# Revit family: Hager-Panelboard_JN_Top-Bottom_Meter_Enclosure-UK-en
name_source: partatom
category: Electrical Equipment
units: mm (PartAtom-declared; Revit-internal decimal feet)

## family parameters
Cut with Voids When Loaded = No
Host = Face
Panel Configuration = Two Columns, Circuits Across
Part Type = Panelboard
Room Calculation Point = No
Round Connector Dimension = Use Diameter
Shared = No

## types (2) — shared parameters
Classification.Uniclass.Pr.Description = Control circuit device enclosures
Classification.Uniclass.Pr.Number = Pr_80_77_28_16
Default Elevation = 1219 mm
EF000003 - Mounting method = EV000384 - Surface mounted (plaster)
EF000007 - Colour = EV000154 - Other
EF000008 - Width = 710 mm
EF000049 - Depth = 160 mm  [stored 0.524934 ft]
EF000118 - With mounting plate = No
EF000339 - Type of cover = EV004216 - Door
EF001062 - EMC-version = No
EF001088 - Extension possible = No
EF001134 - DIN-rail = No
EF001596 - Material housing = EV000179 - Steel
EF004462 - Type of closure = EV000154 - Other
EF005474 - Degree of protection (IP) = EV009848 - IP2XC
EF006244 - Transparent cover/door = No
EF006306 - With lock = No
EF015776 - Earthing terminal block = Yes
EF015941 - Signal passing door = No
Ground Bus = No
HG000001 - Number of columns = 3
HG000002 - With door or cover = Yes
HG000003 - Range = Panelboard Meter Enclosures
HG000005 - Thickness = 3 mm  [stored 0.00984252 ft]
HG000018 - Cut-outs in left = No
HG000019 - Cut-outs in right = No
Manufacturer = Hager
Neutral Bus = No
Type Comments = Panelboard Meter Enclosures
zero-valued in all types: EF000218 - Built-in depth, EF000332 - Built-in height, EF000846 - Built-in width, EF001131 - Internal depth

## per-type parameters (varying)
| type | EF000040 - Height | EF000266 - Number of rows | EF002950 - Width in number of modular spacings | EF015777 - Neutral terminal block | HG000004 - Manufacturer reference | HG000025 - Number of cut-outs | Model |
| Surface mounted P2XC W710 H300 D160 3 Modular spacings - JN3003TM | 300 mm | 1 | 3 | No | JN3003TM | 3 | JN3003TM |
| Surface mounted P2XC W710 H450 D160 6 Modular spacings - JN4506TM | 450 mm  [stored 1.47638 ft] | 2 | 6 | Yes | JN4506TM | 6 | JN4506TM |

note: [stored X ft] marks values corroborated as IEEE doubles in the binary element streams (Revit-internal decimal feet)

## geometry (parser evidence)
native form markers: Sweep x11
no freeform markers — native parametric forms only
